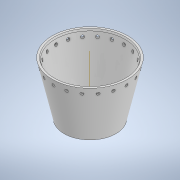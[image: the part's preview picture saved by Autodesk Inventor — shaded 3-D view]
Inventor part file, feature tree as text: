
AUTODESK INVENTOR PART (.ipt)
format: ipt  version: 2021 (Build 250183000, 183)  size: 232,960 bytes
history: native  units: in
note: dims shown in document units (in); Inventor stores cm internally (conversion verified against a paired STEP export)
features: other x19, sketch x4, plane x3, revolve x1, extrude x1, pattern_circular x1, chamfer x1
ambient origin geometry x8: Origin, YZ Plane, XZ Plane, XY Plane, X Axis, Y Axis, Z Axis, Center Point
bodies: Solid1 (feature_tree)
feature tree (30):
  sketch  "Sketch1"  dims[d0=3.1516in d2=3.5433in]
  plane  "Work Plane1"
  sketch  "Sketch2"  dims[d4=4.7244in d6=0.1575in]
  revolve  "Revolution1"  [1 undecoded]
  plane  "Work Plane2"
  extrude  "Extrusion1"  Depth=0.1575in
  pattern_circular  "Circular Pattern1"  Count=6  [1 undecoded]
  chamfer  "Chamfer1"  Distance=0.3937in
  plane  "Work Plane3"
  sketch  "Sketch3"  dims[d7=90.0deg d8=2.3622in]
  sketch  "Sketch4"  dims[d9=0.1969in d10=0.3937in d11=3.937in d12=0.0in d13=7.874in d14=360.0deg d17=1.5758in d18=2.3622in d19=0.1181in d20=0.0787in d21=0.0687in d22=-2.5591in]
  other  "Work Axis1"
  other  "Work Axis2"
  other  "Work Axis3"
  other  "Work Axis4"
  other  "Work Axis5"
  other  "Work Axis6"
  other  "Work Axis7"
  other  "Work Axis8"
  other  "Work Axis9"
  other  "Work Axis10"
  other  "Work Axis11"
  other  "Work Axis12"
  other  "Work Axis13"
  other  "Work Axis14"
  other  "Work Axis15"
  other  "Work Axis16"
  other  "Work Axis17"
  other  "Work Axis18"
  other  "Work Axis19"
note: 2 required parameter values undecoded (feature->parameter linkage not recoverable at this tier; creation-order binding heuristic only, values carry confidence <= 0.55)